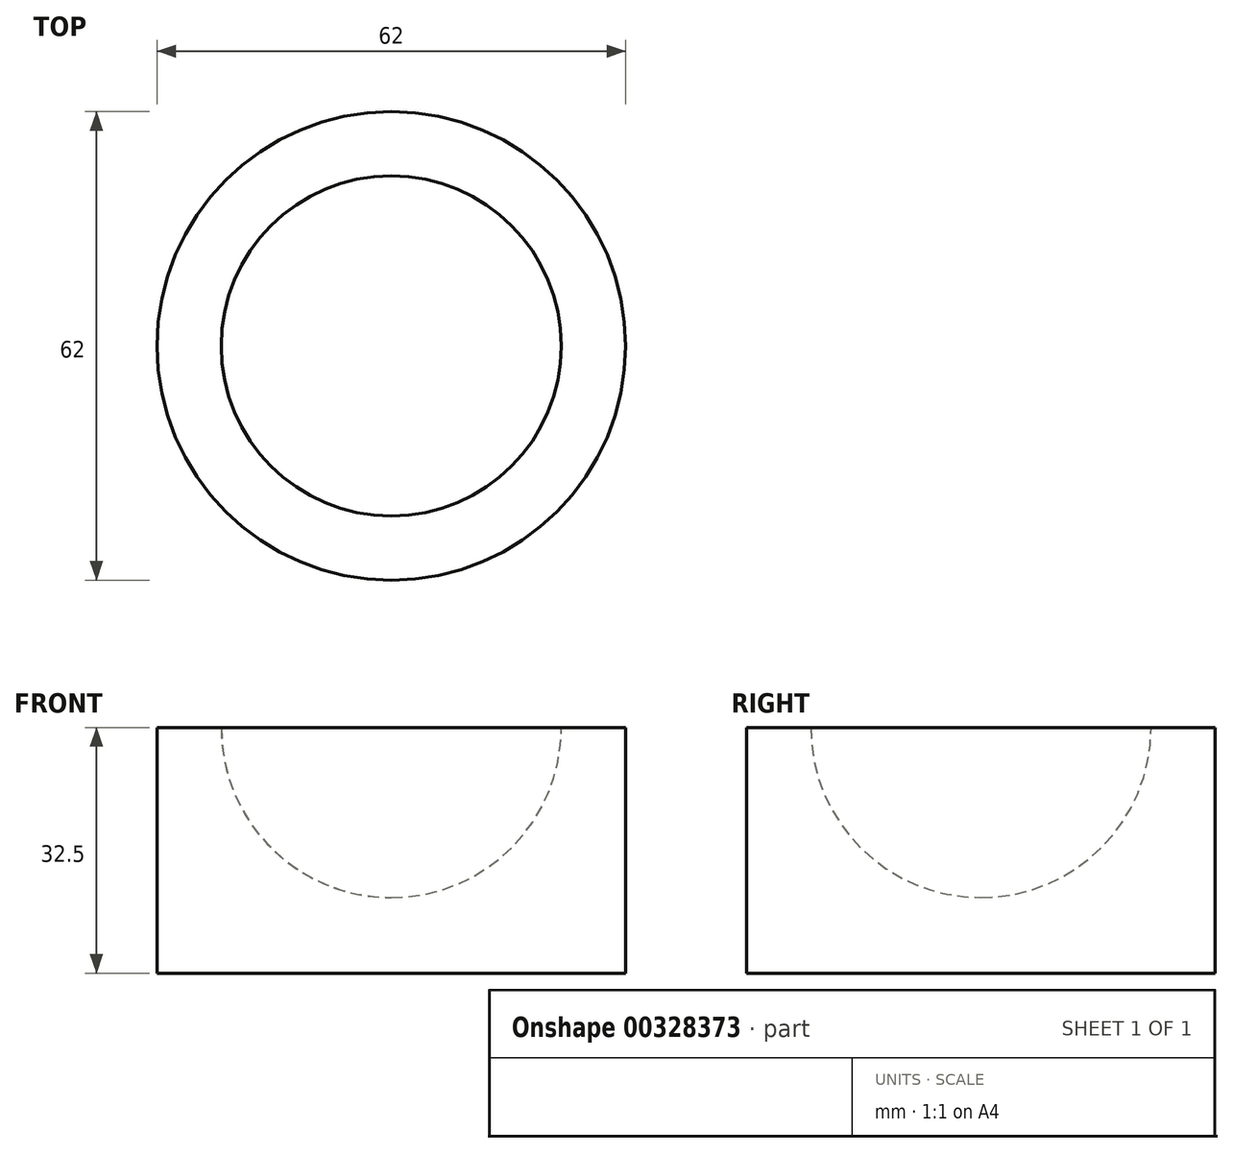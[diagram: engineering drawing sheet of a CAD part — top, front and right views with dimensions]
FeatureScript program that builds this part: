
annotation { "Feature Type Name" : "Feature", "Feature Type Description" : "" }
export const myFeature = defineFeature(function(context is Context, id is Id, definition is map)
    precondition{}
    {
        {
            var Q0;
            Q0=qCreatedBy(makeId("Front.planeOp"),FACE);
            var sketch = newSketch(context, id + "F0", { "sketchPlane" : qUnion([Q0])});
            skLineSegment(sketch, "E0.bottom", {"start": v(0, 0) * mm, "end": v(31, 0) * mm});
            skLineSegment(sketch, "E0.top", {"start": v(0, 32.5) * mm, "end": v(8.5, 32.5) * mm});
            skLineSegment(sketch, "E0.left", {"start": v(0, 0) * mm, "end": v(0, 32.5) * mm});
            skLineSegment(sketch, "E0.right", {"start": v(31, 0) * mm, "end": v(31, 10) * mm});
            skArc(sketch, "E1", {"start": v(8.5, 32.5) * mm, "mid": v(15.1, 16.6) * mm, "end": v(31, 10) * mm});
            skSolve(sketch);
        }
        {
            var Q0;
            Q0 = qSketchRegion(id + "F0", true);
            var Q1;
            Q1=sQuery(id+"F0.wireOp",EDGE,"E0.right");
            revolve(context, id + "F1", {"entities" : qUnion([Q0]), "axis" : qUnion([Q1]), "revolveType" : RevolveType.FULL});
        }
    });
